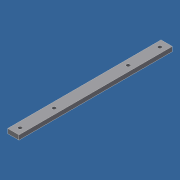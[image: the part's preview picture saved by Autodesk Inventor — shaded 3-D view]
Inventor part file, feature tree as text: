
AUTODESK INVENTOR PART (.ipt)
format: ipt  version: 2015 SP2 (Build 190223200, 223)  size: 92,160 bytes
history: native  units: mm (DEFAULTED — no unit token found)
features: other x8, sketch x1, extrude x1, hole x1
bodies: Solide1 (feature_tree)
feature tree (11):
  other  "Origine"
  sketch  "Esquisse7"
  extrude  "Extrusion3"  Depth=10.0mm
  hole  "Perçage3"  [1 undecoded]
  other  "Plan YZ"
  other  "Plan XZ"
  other  "Plan XY"
  other  "Axe X"
  other  "Axe Y"
  other  "Axe Z"
  other  "Point de centre"
note: 1 required parameter value undecoded (feature->parameter linkage not recoverable at this tier; creation-order binding heuristic only, values carry confidence <= 0.55)
